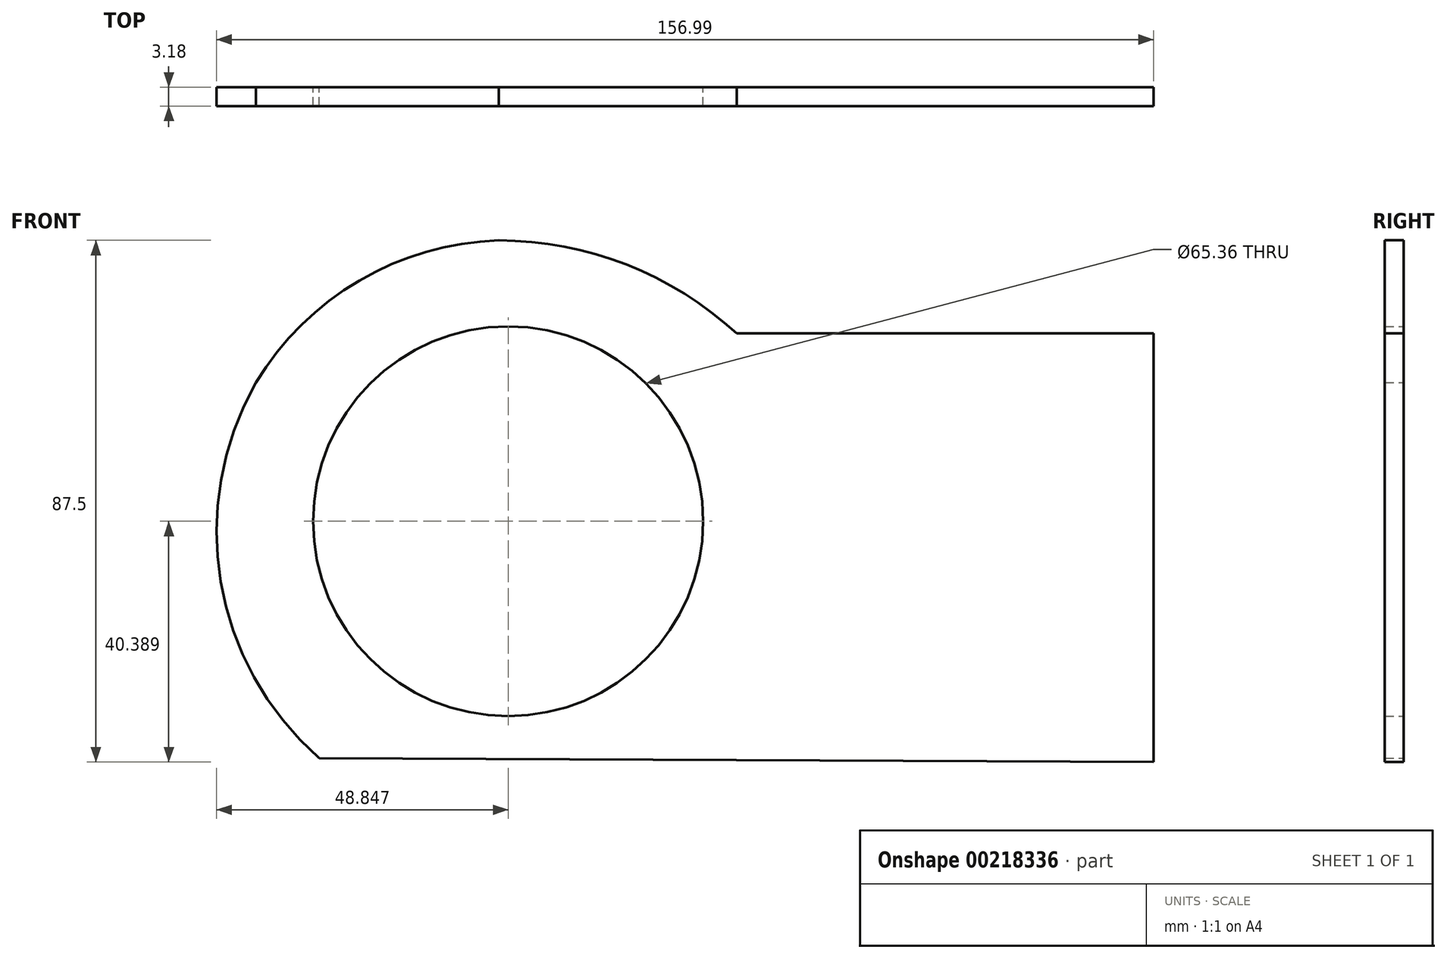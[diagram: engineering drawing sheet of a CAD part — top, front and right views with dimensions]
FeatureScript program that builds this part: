
annotation { "Feature Type Name" : "Feature", "Feature Type Description" : "" }
export const myFeature = defineFeature(function(context is Context, id is Id, definition is map)
    precondition{}
    {
        {
            var Q0;
            Q0=qCreatedBy(makeId("Front.planeOp"),FACE);
            var sketch = newSketch(context, id + "F0", { "sketchPlane" : qUnion([Q0])});
            skLineSegment(sketch, "E0", {"start": v(52.8, 27.63) * mm, "end": v(52.8, -44.25) * mm});
            skLineSegment(sketch, "E1", {"start": v(52.8, -44.25) * mm, "end": v(-87, -43.59) * mm});
            skLineSegment(sketch, "E2", {"start": v(52.8, 27.63) * mm, "end": v(-17.01, 27.63) * mm});
            skArc(sketch, "E3", {"start": v(-97.6, 19.4) * mm, "mid": v(-103.5, -13.98) * mm, "end": v(-87, -43.59) * mm});
            skArc(sketch, "E4", {"start": v(-56.92, 43.25) * mm, "mid": v(-80.3, 36.5) * mm, "end": v(-97.6, 19.4) * mm});
            skArc(sketch, "E5", {"start": v(-17.01, 27.63) * mm, "mid": v(-35.5, 39.19) * mm, "end": v(-56.92, 43.25) * mm});
            skCircle(sketch, "E6", {"center": v(-55.34, -3.86) * mm, "radius": 32.68 * mm});
            skSolve(sketch);
        }
        {
            var Q0;
            Q0 = qSketchRegion(id + "F0", true);
            extrude(context, id + "F1", {"entities" : qUnion([Q0]), "depth" : 3.17 * mm});
        }
    });
